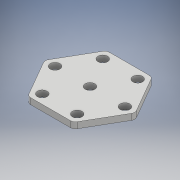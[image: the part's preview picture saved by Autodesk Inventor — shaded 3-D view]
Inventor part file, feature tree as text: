
AUTODESK INVENTOR PART (.ipt)
format: ipt  version: 2017 (Build 210142000, 142)  size: 133,632 bytes
history: native  units: mm
features: extrude x1, fillet x1, sketch x1
ambient origin geometry x8: Origin, YZ Plane, XZ Plane, XY Plane, X Axis, Y Axis, Z Axis, Center Point
bodies: Solid1 (feature_tree)
feature tree (3):
  extrude  "Extrusion1"  Depth=4.0mm
  fillet  "Fillet1"  Radius=8.0mm
  sketch  "Sketch1"  dims[d0=22.0mm d1=50.0mm d2=8.0mm d3=65.0mm d4=8.0mm d5=5.0mm d6=0.0mm d7=4.0mm]
